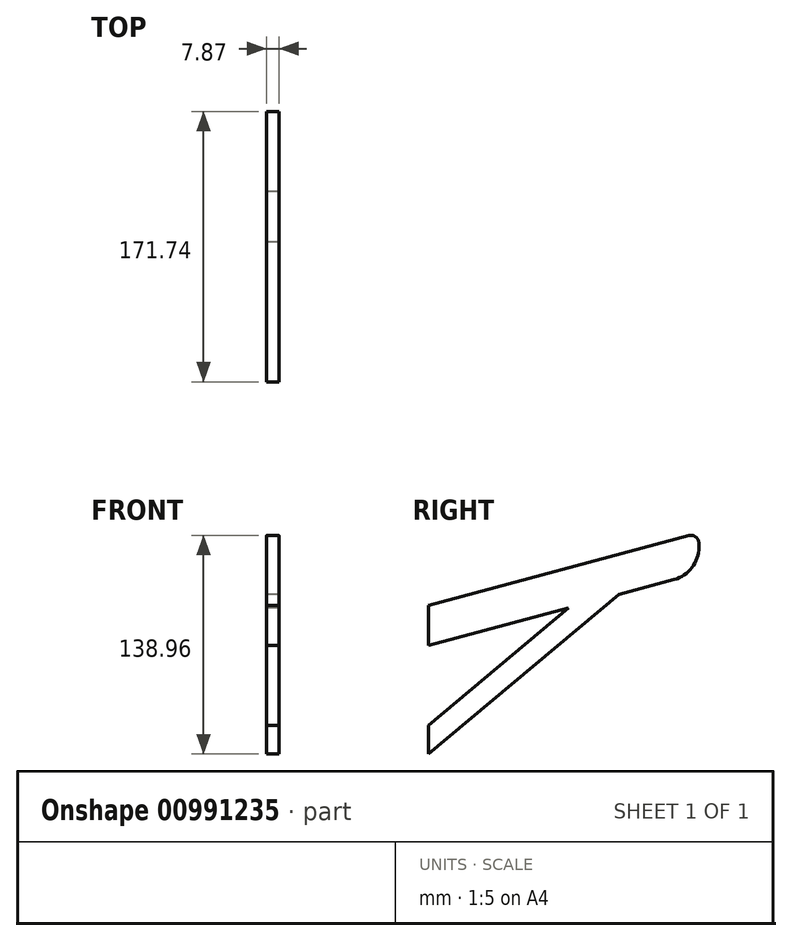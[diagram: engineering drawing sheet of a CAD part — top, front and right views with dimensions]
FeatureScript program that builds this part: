
annotation { "Feature Type Name" : "Feature", "Feature Type Description" : "" }
export const myFeature = defineFeature(function(context is Context, id is Id, definition is map)
    precondition{}
    {
        {
            var Q0;
            Q0=qCreatedBy(makeId("Right.planeOp"),FACE);
            var sketch = newSketch(context, id + "F0", { "sketchPlane" : qUnion([Q0])});
            skLineSegment(sketch, "E0", {"start": v(0, 0) * mm, "end": v(0, 25.4) * mm});
            skLineSegment(sketch, "E1", {"start": v(171.74, 46.02) * mm, "end": v(171.74, 71.42) * mm});
            skLineSegment(sketch, "E2", {"start": v(171.74, 71.42) * mm, "end": v(0, 25.4) * mm});
            skLineSegment(sketch, "E3", {"start": v(171.74, 46.02) * mm, "end": v(0, 0) * mm});
            skLineSegment(sketch, "E4", {"start": v(0, -69.08) * mm, "end": v(120.94, 32.4) * mm});
            skLineSegment(sketch, "E5", {"start": v(88.9, 23.82) * mm, "end": v(0, -50.78) * mm});
            skLineSegment(sketch, "E6", {"start": v(0, -50.78) * mm, "end": v(0, -69.08) * mm});
            skSolve(sketch);
        }
        {
            var Q0;
            Q0=makeQuery(id+"F0.imprint","IMPRINT",FACE,{"disambiguationData":[TD([[makeQuery(id+"F0.imprint","IMPRINT",EDGE,{"derivedFrom":sQuery(id+"F0.wireOp",EDGE,"E0")}),-1.0]])]});
            var Q1;
            Q1=makeQuery(id+"F0.imprint","IMPRINT",FACE,{"disambiguationData":[TD([[makeQuery(id+"F0.imprint","IMPRINT",EDGE,{"derivedFrom":sQuery(id+"F0.wireOp",EDGE,"E4")}),1.0]])]});
            extrude(context, id + "F1", {"entities" : qUnion([Q0, Q1]), "depth" : 7.87 * mm, "offsetDistance" : 25.4 * mm});
        }
        {
            var Q0;
            Q0=makeQuery(id+"F1.opExtrude","SWEPT_EDGE",EDGE,{"disambiguationData":[OSD([sQuery(id+"F0.wireOp",EDGE,"E1"),sQuery(id+"F0.wireOp",EDGE,"E3")])]});
            fillet(context, id + "F2", {"entities" : qUnion([Q0]), "radius" : 21.29 * mm, "tangentPropagation" : true, "allowEdgeOverflow" : false});
        }
        {
            var Q0;
            Q0=makeQuery(id+"F1.opExtrude","SWEPT_EDGE",EDGE,{"disambiguationData":[OSD([sQuery(id+"F0.wireOp",EDGE,"E1"),sQuery(id+"F0.wireOp",EDGE,"E2")])]});
            fillet(context, id + "F3", {"entities" : qUnion([Q0]), "radius" : 5.08 * mm, "tangentPropagation" : true, "allowEdgeOverflow" : false});
        }
    });
